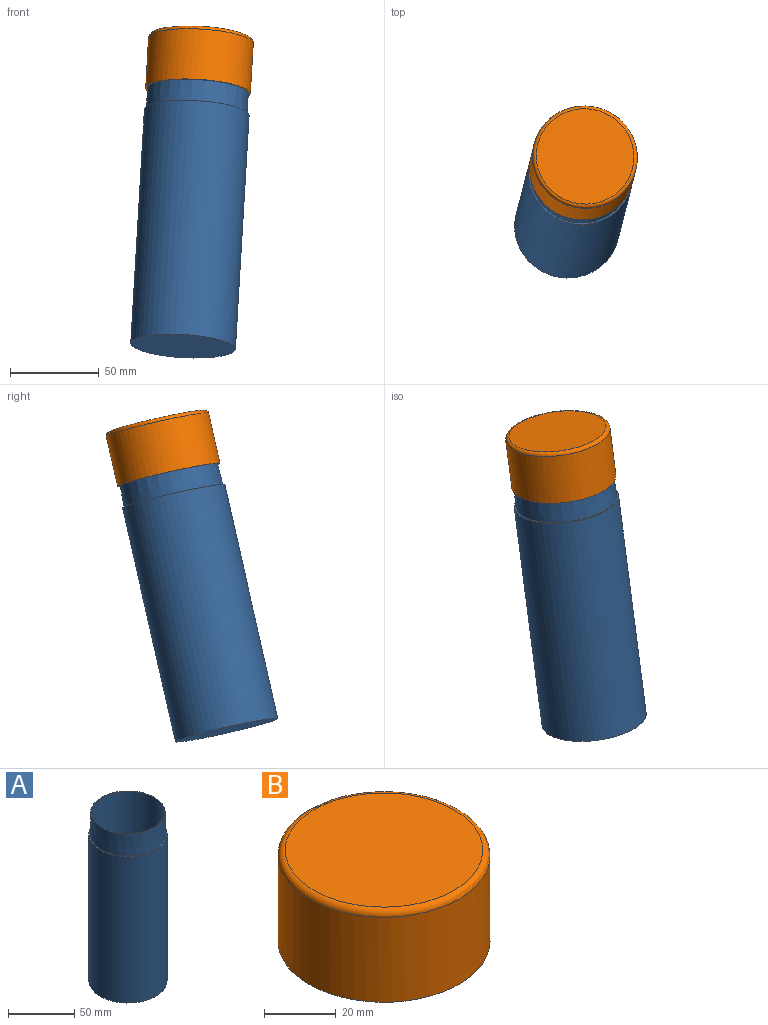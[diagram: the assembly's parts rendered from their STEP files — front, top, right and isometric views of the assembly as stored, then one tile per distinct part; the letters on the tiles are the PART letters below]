
ASSEMBLY  parts=2 mates=1
PART A: 7 faces, bbox 59x59x155 mm
  f0: plane 59x59mm, normal (0,0,1), area 182.2mm2, adj f1,f4
  f1: cylinder r=29.5mm len=135mm, axis (0,0,-1), area 25022.8mm2, adj f0,f2
  f2: plane 59x59mm, normal (0,0,-1), area 2734mm2, adj f1
  f3: plane 56.3x56.3mm, normal (0,0,1), area 113.8mm2, adj f4,f6
  f4: cone r=28.5mm half-angle=1deg, axis (0,0,-1), area 3560mm2, adj f0,f3
  f5: plane 55x55mm, normal (0,0,1), area 2375.8mm2, adj f6
  f6: cylinder r=27.5mm len=153mm, axis (0,0,-1), area 26436.5mm2, adj f3,f5
PART B: 6 faces, bbox 63.9x63.9x31 mm
  f0: cylinder r=29.5mm len=59mm, axis (0,0,-1), area 5375.3mm2, adj f1,f5
  f1: plane 59x59mm, normal (0,0,-1), area 164.3mm2, adj f0,f2
  f2: cylinder r=28.6mm len=57.2mm, axis (0,0,-1), area 5229.2mm2, adj f1,f3
  f3: plane 57.2x57.2mm, normal (0,0,-1), area 2569.7mm2, adj f2
  f4: plane 55x55mm, normal (0,0,1), area 2375.8mm2, adj f5
  f5: torus R=27.5mm, axis (0,0,1), area 568mm2, adj f0,f4
PLACE A rot(axis=(-0.03,-0.11,-0.99),179.6deg) t=(-1.82,-31.47,43.4)mm
PLACE B rot(axis=(-0.03,-0.11,-0.99),179.6deg) t=(-1.11,-28.74,55.43)mm
MATE cylindrical A.f1 <-> B.f0  axis (0.06,0.22,0.97) through (5.87,-1.71,174.85)mm
